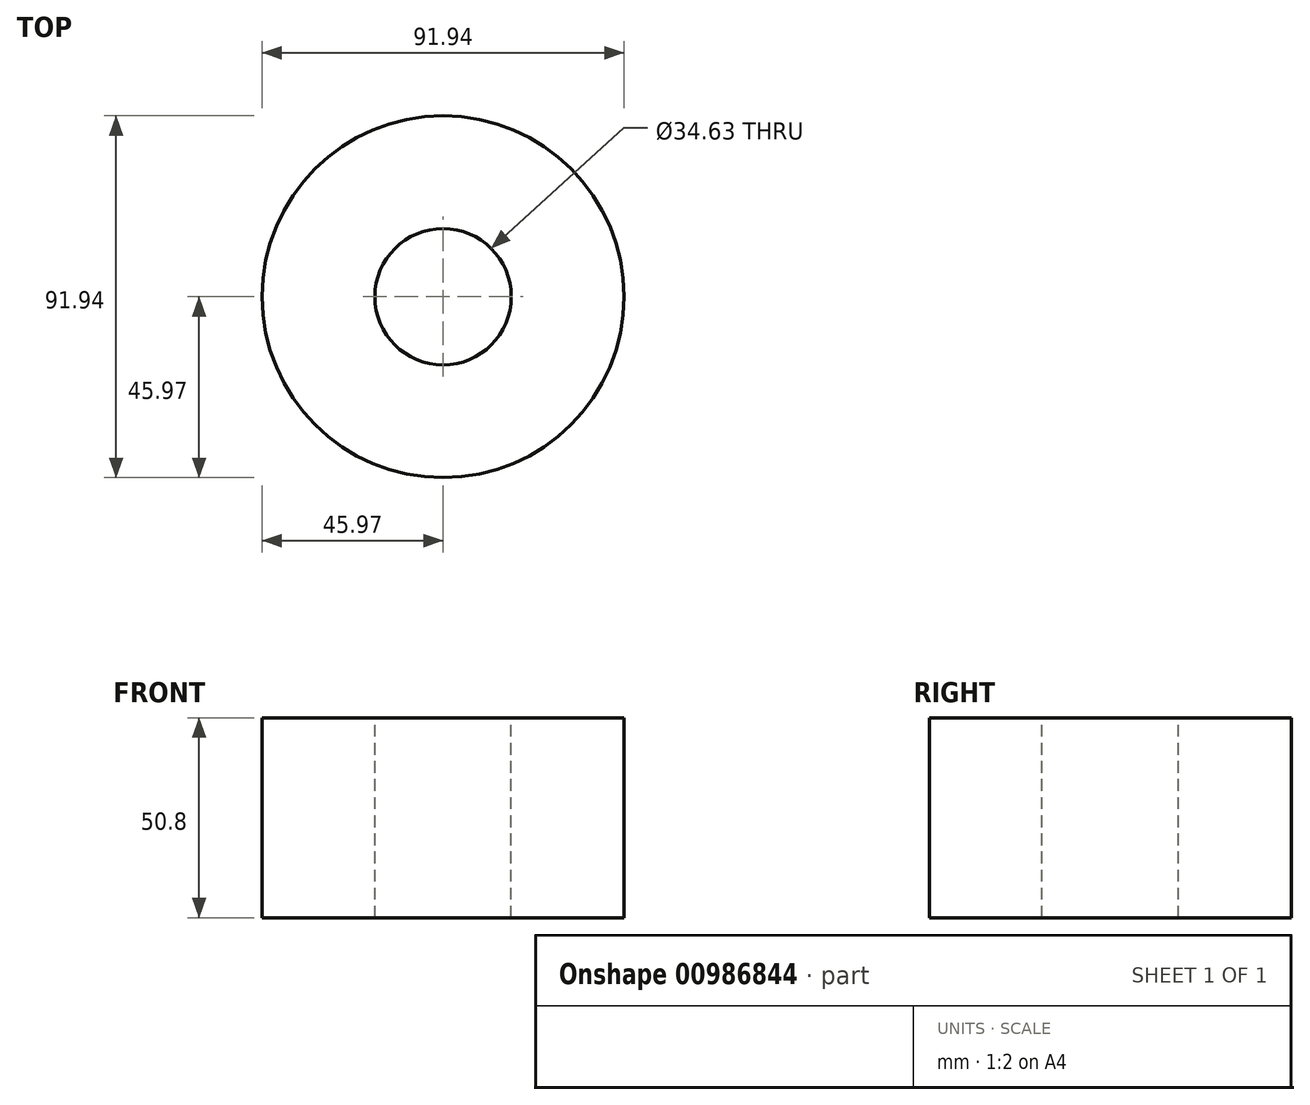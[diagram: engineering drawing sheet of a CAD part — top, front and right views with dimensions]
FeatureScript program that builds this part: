
annotation { "Feature Type Name" : "Feature", "Feature Type Description" : "" }
export const myFeature = defineFeature(function(context is Context, id is Id, definition is map)
    precondition{}
    {
        {
            var Q0;
            Q0=qCreatedBy(makeId("Top.planeOp"),FACE);
            var sketch = newSketch(context, id + "F0", { "sketchPlane" : qUnion([Q0])});
            skCircle(sketch, "E0", {"center": v(0, 0) * mm, "radius": 45.97 * mm});
            skSolve(sketch);
        }
        {
            var Q0;
            Q0=makeQuery(id+"F0.imprint","IMPRINT",FACE,{"disambiguationData":[TD([[makeQuery(id+"F0.imprint","IMPRINT",EDGE,{"derivedFrom":sQuery(id+"F0.wireOp",EDGE,"E0")}),1.0]])]});
            extrude(context, id + "F1", {"entities" : qUnion([Q0]), "depth" : 50.8 * mm, "offsetDistance" : 25.4 * mm});
        }
        {
            var Q0;
            Q0=makeQuery(id+"F1.opExtrude","CAP_FACE",FACE,{"disambiguationData":[OSD([sQuery(id+"F0.wireOp",EDGE,"E0")])],"isStart":false});
            var sketch = newSketch(context, id + "F2", { "sketchPlane" : qUnion([Q0])});
            skCircle(sketch, "E1", {"center": v(0, 0) * mm, "radius": 17.32 * mm});
            skSolve(sketch);
        }
        {
            var Q0;
            Q0=makeQuery(id+"F2.imprint","IMPRINT",FACE,{"disambiguationData":[TD([[makeQuery(id+"F2.imprint","IMPRINT",EDGE,{"derivedFrom":sQuery(id+"F2.wireOp",EDGE,"E1")}),1.0]])]});
            var Q1;
            Q1=sQuery(id+"F2.wireOp",EDGE,"E1");
            extrude(context, id + "F3", {"entities" : qUnion([Q0]), "operationType" : NewBodyOperationType.REMOVE, "surfaceOperationType" : NewSurfaceOperationType.ADD, "surfaceEntities" : qUnion([Q1]), "endBound" : BoundingType.THROUGH_ALL, "oppositeDirection" : true, "depth" : 25.4 * mm, "offsetDistance" : 25.4 * mm});
        }
    });
